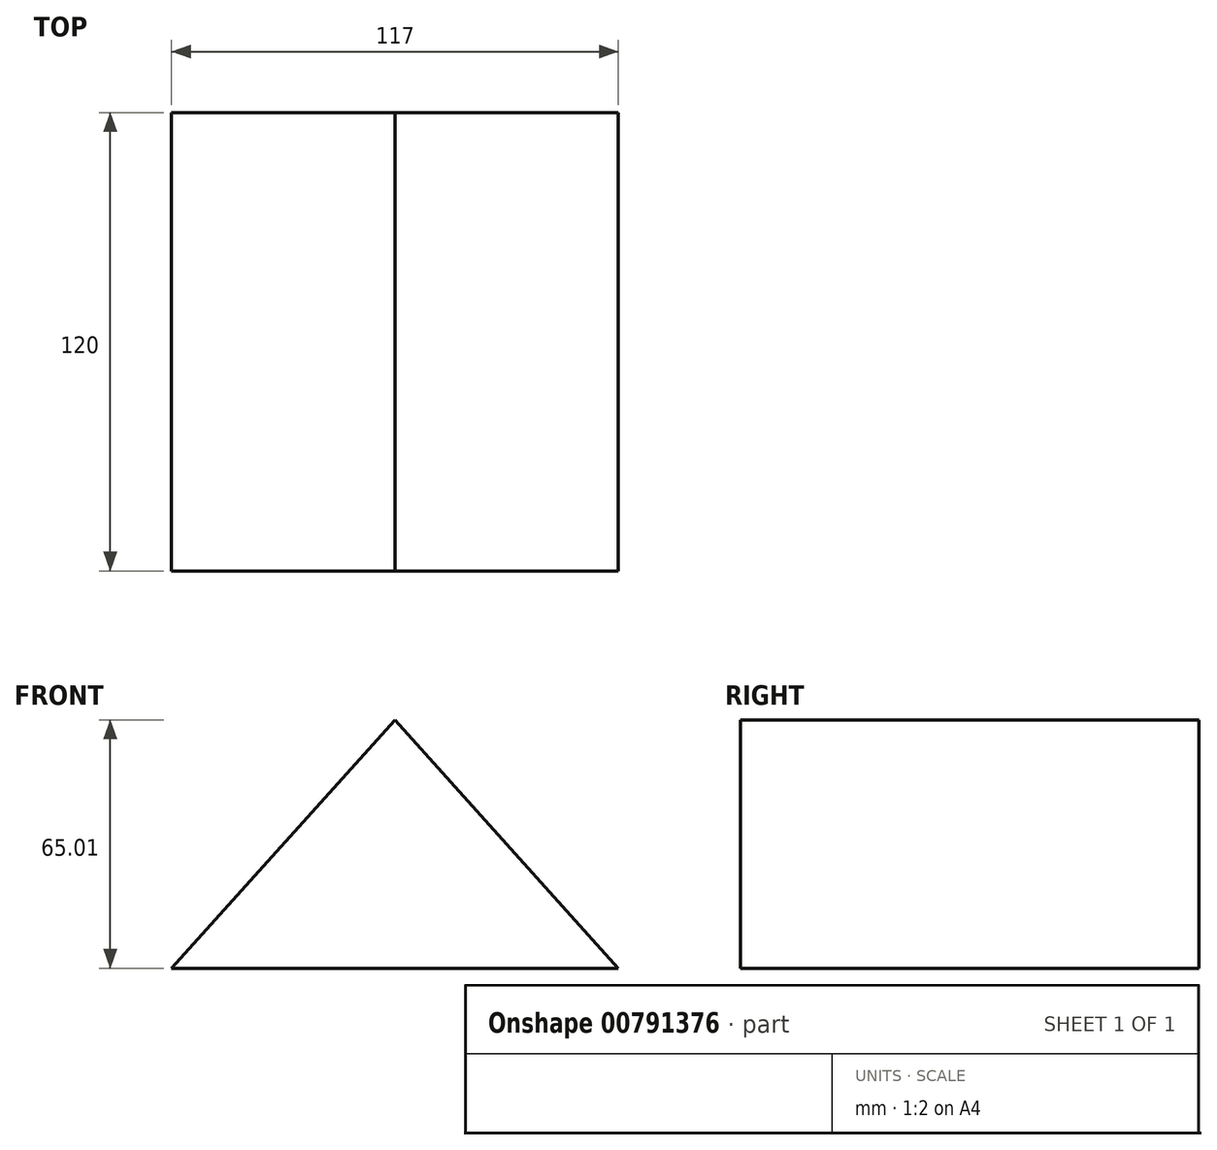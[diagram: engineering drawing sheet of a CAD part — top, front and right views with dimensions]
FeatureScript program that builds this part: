
annotation { "Feature Type Name" : "Feature", "Feature Type Description" : "" }
export const myFeature = defineFeature(function(context is Context, id is Id, definition is map)
    precondition{}
    {
        {
            var Q0;
            Q0=qCreatedBy(makeId("Front.planeOp"),FACE);
            var sketch = newSketch(context, id + "F0", { "sketchPlane" : qUnion([Q0])});
            skLineSegment(sketch, "E0", {"start": v(-32.1, -41.36) * mm, "end": v(84.9, -41.36) * mm});
            skLineSegment(sketch, "E1", {"start": v(84.9, -41.36) * mm, "end": v(26.4, 23.65) * mm});
            skPoint(sketch, "E1.endSnap0", {"position": v(26.4, -41.36) * mm});
            skLineSegment(sketch, "E2", {"start": v(26.4, 23.65) * mm, "end": v(-32.1, -41.36) * mm});
            skSolve(sketch);
        }
        {
            var Q0;
            Q0 = qSketchRegion(id + "F0", true);
            extrude(context, id + "F1", {"entities" : qUnion([Q0]), "depth" : 120 * mm, "offsetDistance" : 25 * mm});
        }
    });
